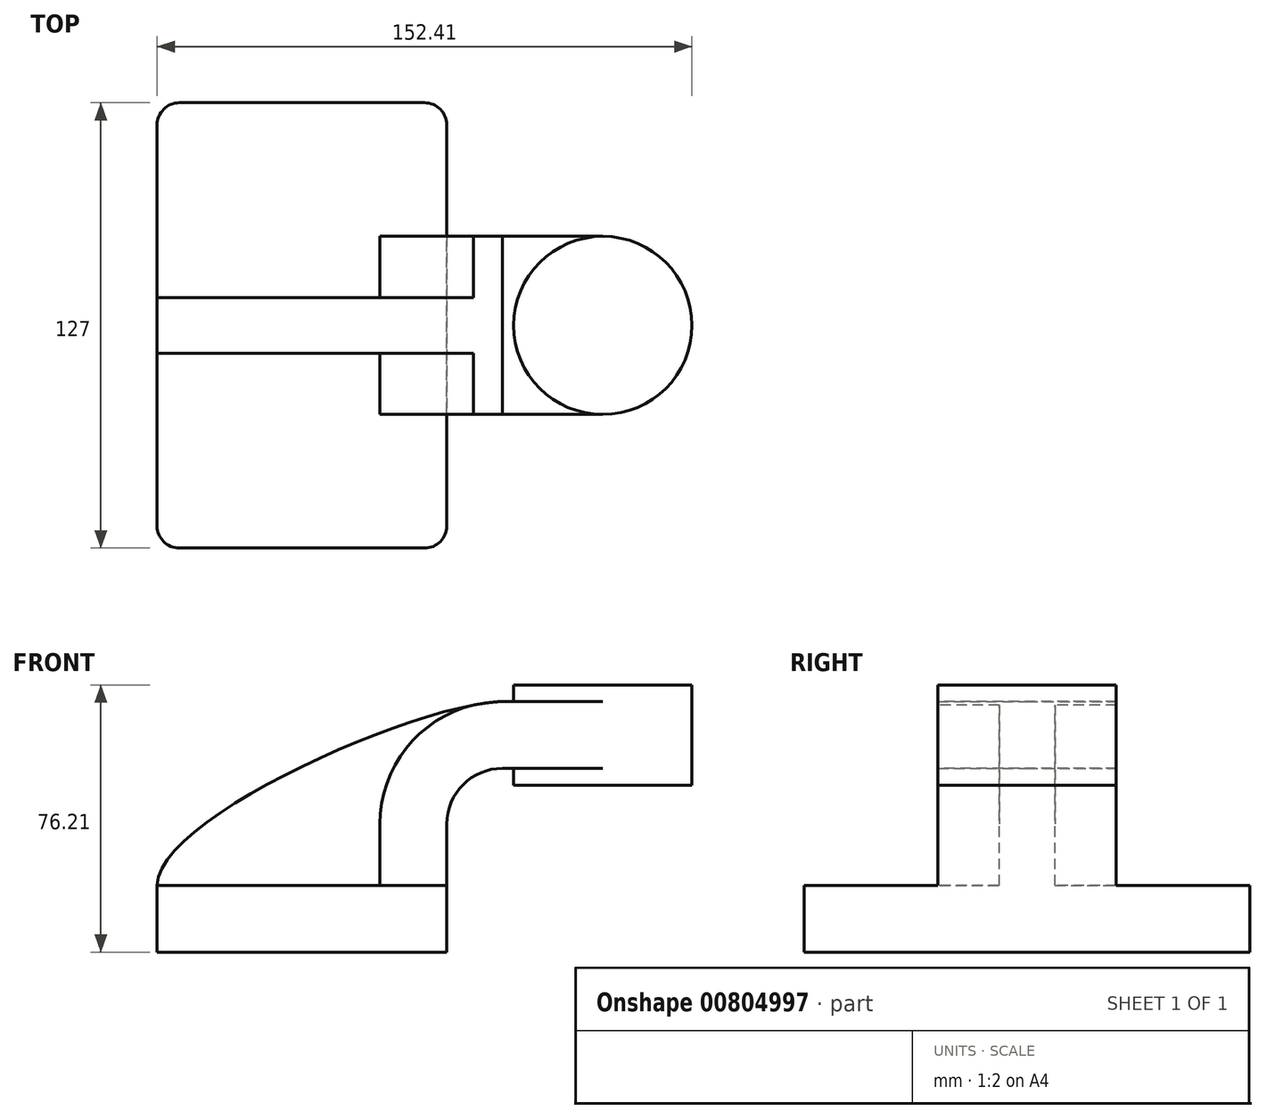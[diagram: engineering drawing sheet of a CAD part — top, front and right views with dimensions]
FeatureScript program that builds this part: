
annotation { "Feature Type Name" : "Feature", "Feature Type Description" : "" }
export const myFeature = defineFeature(function(context is Context, id is Id, definition is map)
    precondition{}
    {
        {
            var Q0;
            Q0=qCreatedBy(makeId("Front.planeOp"),FACE);
            var sketch = newSketch(context, id + "F0", { "sketchPlane" : qUnion([Q0])});
            skLineSegment(sketch, "E0.bottom", {"start": v(-41.28, -9.52) * mm, "end": v(41.28, -9.52) * mm});
            skLineSegment(sketch, "E0.top", {"start": v(-41.28, 9.53) * mm, "end": v(41.27, 9.53) * mm});
            skLineSegment(sketch, "E0.left", {"start": v(-41.27, -9.52) * mm, "end": v(-41.28, 9.53) * mm});
            skLineSegment(sketch, "E0.right", {"start": v(41.28, -9.52) * mm, "end": v(41.27, 9.53) * mm});
            skPoint(sketch, "E0.middle", {"position": v(0, 0) * mm});
            skLineSegment(sketch, "E1.bottom", {"start": v(60.32, 38.1) * mm, "end": v(111.12, 38.1) * mm});
            skLineSegment(sketch, "E1.top", {"start": v(60.32, 66.67) * mm, "end": v(111.12, 66.67) * mm});
            skLineSegment(sketch, "E1.left", {"start": v(60.32, 38.1) * mm, "end": v(60.32, 66.67) * mm});
            skLineSegment(sketch, "E1.right", {"start": v(111.13, 38.1) * mm, "end": v(111.12, 66.67) * mm});
            skPoint(sketch, "E1.middle", {"position": v(85.72, 52.39) * mm});
            skLineSegment(sketch, "E2", {"start": v(41.27, 9.53) * mm, "end": v(41.27, 27) * mm});
            skArc(sketch, "E3", {"start": v(41.27, 27) * mm, "mid": v(45.92, 38.23) * mm, "end": v(57.15, 42.88) * mm});
            skLineSegment(sketch, "E4", {"start": v(57.15, 42.88) * mm, "end": v(85.72, 42.88) * mm});
            skLineSegment(sketch, "E5.0", {"start": v(57.15, 61.93) * mm, "end": v(85.72, 61.93) * mm});
            skArc(sketch, "E5.1", {"start": v(22.22, 27) * mm, "mid": v(32.45, 51.7) * mm, "end": v(57.15, 61.93) * mm});
            skLineSegment(sketch, "E5.2", {"start": v(22.22, 9.53) * mm, "end": v(22.22, 27) * mm});
            skLineSegment(sketch, "E6", {"start": v(85.72, 38.1) * mm, "end": v(85.72, 66.67) * mm});
            skPoint(sketch, "E6.endSnap0", {"position": v(85.72, 66.67) * mm});
            skFitSpline(sketch, "E7", {"points": [v(-41.28, 9.53) * mm, v(57.15, 61.93) * mm], "startDerivative": vector(0.04, 57.52) * mm, "endDerivative": vector(75.26, 1.95) * mm});
            skSolve(sketch);
        }
        {
            var Q0;
            Q0=makeQuery(id+"F0.imprint","IMPRINT",FACE,{"disambiguationData":[TD([[makeQuery(id+"F0.imprint","IMPRINT",EDGE,{"derivedFrom":sQuery(id+"F0.wireOp",EDGE,"E0.bottom")}),1.0]])]});
            extrude(context, id + "F1", {"entities" : qUnion([Q0]), "endBound" : BoundingType.SYMMETRIC, "depth" : 127 * mm, "offsetDistance" : 25.4 * mm});
        }
        {
            var Q0;
            {var subQ1=sQuery(id+"F0.wireOp",EDGE,"E2");Q0=makeQuery(id+"F0.imprint","IMPRINT",FACE,{"disambiguationData":[TD([[makeQuery(id+"F0.imprint","IMPRINT",EDGE,{"derivedFrom":subQ1}),1.0]])]});}
            var Q1;
            Q1 = qSketchRegion(id + "FveaqtFkseZuOdv_0", true);
            extrude(context, id + "F2", {"entities" : qUnion([Q0, Q1]), "operationType" : NewBodyOperationType.ADD, "endBound" : BoundingType.SYMMETRIC, "oppositeDirection" : true, "depth" : 50.8 * mm, "offsetDistance" : 25.4 * mm});
        }
        {
            var Q0;
            {var subQ3=sQuery(id+"F0.wireOp",EDGE,"E5.2");Q0=makeQuery(id+"F0.imprint","IMPRINT",FACE,{"disambiguationData":[TD([[makeQuery(id+"F0.imprint","IMPRINT",EDGE,{"derivedFrom":subQ3}),1.0]])]});}
            extrude(context, id + "F3", {"entities" : qUnion([Q0]), "operationType" : NewBodyOperationType.ADD, "endBound" : BoundingType.SYMMETRIC, "depth" : 15.88 * mm, "offsetDistance" : 25.4 * mm});
        }
        {
            var Q0;
            {var subQ0=sQuery(id+"F0.wireOp",EDGE,"E4");var subQ1=sQuery(id+"F0.wireOp",EDGE,"E1.left");var subQ2=makeQuery(id+"F0.imprint","INTERSECT",VERTEX,{"derivedFrom":[subQ1,subQ0]});Q0=makeQuery(id+"F0.imprint","IMPRINT",FACE,{"disambiguationData":[TD([[makeQuery(id+"F0.imprint","IMPRINT",EDGE,{"disambiguationData":[TD([[subQ2,-1.0]])],"derivedFrom":subQ1}),-1.0]])]});}
            extrude(context, id + "F4", {"entities" : qUnion([Q0]), "operationType" : NewBodyOperationType.ADD, "endBound" : BoundingType.SYMMETRIC, "depth" : 50.8 * mm, "offsetDistance" : 25.4 * mm});
        }
        {
            var Q0;
            {var subQ4=sQuery(id+"F0.wireOp",EDGE,"E1.right");Q0=makeQuery(id+"F0.imprint","IMPRINT",FACE,{"disambiguationData":[TD([[makeQuery(id+"F0.imprint","IMPRINT",EDGE,{"derivedFrom":subQ4}),1.0]])]});}
            var Q1;
            Q1=sQuery(id+"F0.wireOp",EDGE,"E6");
            revolve(context, id + "F5", {"operationType" : NewBodyOperationType.ADD, "surfaceOperationType" : NewSurfaceOperationType.NEW, "entities" : qUnion([Q0]), "axis" : qUnion([Q1]), "revolveType" : RevolveType.FULL});
        }
        {
            var Q0;
            Q0=makeQuery(id+"F1.opExtrude","CAP_EDGE",EDGE,{"disambiguationData":[OSD([sQuery(id+"F0.wireOp",EDGE,"E0.right")])],"isStart":true});
            var Q1;
            Q1=makeQuery(id+"F1.opExtrude","CAP_EDGE",EDGE,{"disambiguationData":[OSD([sQuery(id+"F0.wireOp",EDGE,"E0.right")])],"isStart":false});
            var Q2;
            Q2=makeQuery(id+"F1.opExtrude","CAP_EDGE",EDGE,{"disambiguationData":[OSD([sQuery(id+"F0.wireOp",EDGE,"E0.left")])],"isStart":false});
            var Q3;
            Q3=makeQuery(id+"F1.opExtrude","CAP_EDGE",EDGE,{"disambiguationData":[OSD([sQuery(id+"F0.wireOp",EDGE,"E0.left")])],"isStart":true});
            fillet(context, id + "F6", {"entities" : qUnion([Q0, Q1, Q2, Q3]), "radius" : 6.35 * mm, "tangentPropagation" : true, "allowEdgeOverflow" : false});
        }
    });
